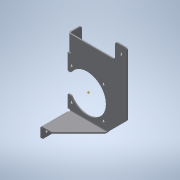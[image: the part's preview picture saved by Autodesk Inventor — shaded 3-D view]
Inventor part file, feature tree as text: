
AUTODESK INVENTOR PART (.ipt)
format: ipt  version: 2022.1 (Build 261234000, 234)  size: 253,952 bytes
history: native  units: mm
features: other x12, sheet_metal_op x8, reference x7, sketch x6, chamfer x3, hole x2
ambient origin geometry x8: Origin, YZ Plane, XZ Plane, XY Plane, X Axis, Y Axis, Z Axis, Center Point
bodies: Solid1 (feature_tree)
feature tree (38):
  sheet_metal_op  "Face1"
  sheet_metal_op  "Face2"
  sheet_metal_op  "Face3"
  sheet_metal_op  "Flange1"
  hole  "Hole1"  [1 undecoded]
  hole  "Hole2"  [1 undecoded]
  chamfer  "Corner Round1"
  chamfer  "Corner Round2"
  chamfer  "Corner Round3"
  other  "Corner Chamfer1"
  sketch  "Sketch1"  dims[d6=3.0mm d9=45.0deg]
  reference  "Reference3"
  reference  "Reference4"
  other  "Plate1"
  reference  "Reference5"
  reference  "Reference6"
  reference  "Reference7"
  reference  "Reference8"
  reference  "Reference9"
  sketch  "Sketch3"  dims[d10=210.0mm d11=30.0mm]
  other  "Plate2"
  sheet_metal_op  "Bend1"
  sketch  "Sketch4"  dims[d13=96.0mm]
  other  "Plate3"
  sheet_metal_op  "Bend2"
  sketch  "Sketch5"  dims[d18=40.0mm]
  other  "Plate4"
  sheet_metal_op  "Bend3"
  sheet_metal_op  "Corner1"
  sketch  "Sketch6"  dims[d21=3.0mm]
  sketch  "Sketch7"  dims[d22=3.0mm d23=1.5mm d24=6.0mm d25=3.0mm d28=3.0mm d29=3.0mm d30=1.5mm d31=6.0mm d32=3.0mm d33=3.0mm d34=1.5mm d35=6.0mm d36=3.0mm d37=30.0mm d38=90.0deg d39=3.0mm d40=12.0mm d41=3.0mm d42=3.0mm d43=50.0mm d44=6.6mm d45=6.0mm d46=12.6mm d47=2.0mm d48=90.0deg d49=3.0mm d50=20.594885mm d51=50.0mm d52=40.0mm d53=6.6mm d54=6.0mm d55=4.0mm d56=2.0mm d57=90.0deg d58=8.0mm d59=20.594885mm d60=6.0mm d61=6.0mm d62=2.0mm d63=4.0mm d64=6.0mm d65=45.0deg d66=120.0mm d67=100.0mm d68=40.0mm d69=30.0mm d70=70.0mm d71=45.0deg]
  other  "RobotPallet.iam"
  other  "EstructuraInferior:1"
  other  "Frame_Base:1"
  other  "ISO 10799-2 40x40x2 - 437.5:2"
  other  "ISO 10799-2 40x40x2 - 2899.41:1"
  other  "BL Motor + Encoder + Gearbox + Rueda:2"
  other  "bg-95x80-885950205312:1"
note: 2 required parameter values undecoded (feature->parameter linkage not recoverable at this tier; creation-order binding heuristic only, values carry confidence <= 0.55)
